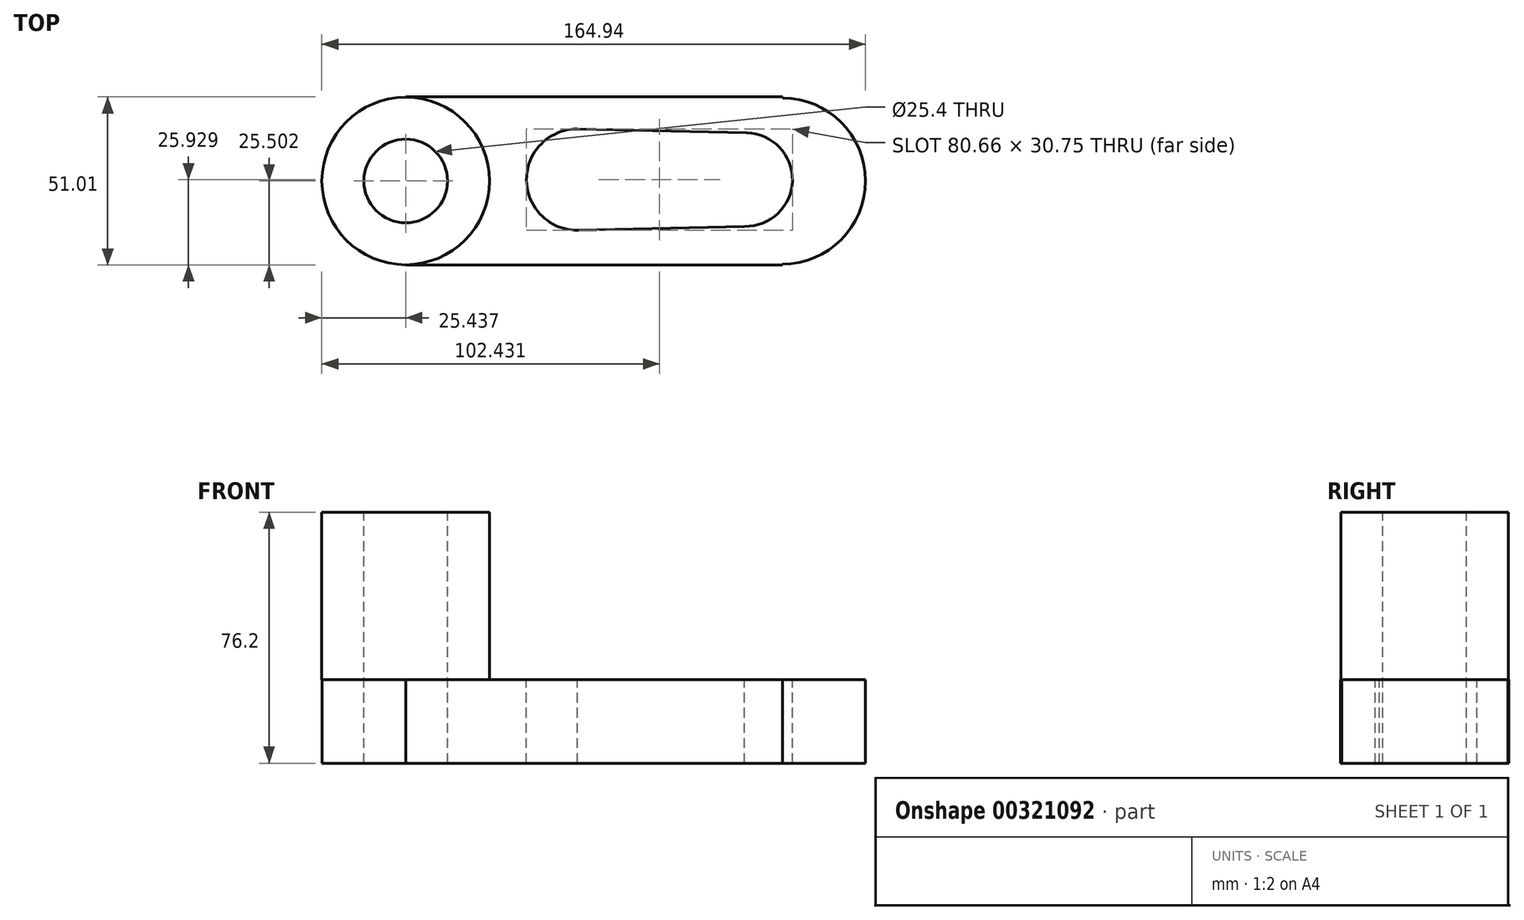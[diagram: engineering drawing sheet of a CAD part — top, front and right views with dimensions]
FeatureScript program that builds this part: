
annotation { "Feature Type Name" : "Feature", "Feature Type Description" : "" }
export const myFeature = defineFeature(function(context is Context, id is Id, definition is map)
    precondition{}
    {
        {
            var Q0;
            Q0=qCreatedBy(makeId("Top.planeOp"),FACE);
            var sketch = newSketch(context, id + "F0", { "sketchPlane" : qUnion([Q0])});
            skLineSegment(sketch, "E0.bottom", {"start": v(-52.04, 27.92) * mm, "end": v(62.26, 27.92) * mm});
            skLineSegment(sketch, "E0.top", {"start": v(-52.04, -23.1) * mm, "end": v(62.26, -23.1) * mm});
            skLineSegment(sketch, "E0.left", {"start": v(-52.04, 27.92) * mm, "end": v(-52.04, 27.77) * mm});
            skLineSegment(sketch, "E0.right", {"start": v(62.26, 27.92) * mm, "end": v(62.26, 27.61) * mm});
            skArc(sketch, "E1", {"start": v(-52.04, 27.77) * mm, "mid": v(-77.4, 2.41) * mm, "end": v(-52.04, -22.95) * mm});
            skArc(sketch, "E2", {"start": v(62.26, -22.79) * mm, "mid": v(87.46, 2.41) * mm, "end": v(62.26, 27.61) * mm});
            skLineSegment(sketch, "E3.trimOffspring", {"start": v(-52.04, -22.95) * mm, "end": v(-52.04, -23.1) * mm});
            skLineSegment(sketch, "E4.trimOffspring", {"start": v(62.26, -22.79) * mm, "end": v(62.26, -23.1) * mm});
            skSolve(sketch);
        }
        {
            var Q0;
            Q0 = qSketchRegion(id + "F0", true);
            extrude(context, id + "F1", {"entities" : qUnion([Q0]), "depth" : 25.4 * mm});
        }
        {
            var Q0;
            Q0=makeQuery(id+"F1.opExtrude","CAP_FACE",FACE,{"disambiguationData":[OSD([sQuery(id+"F0.wireOp",EDGE,"E0.bottom"),sQuery(id+"F0.wireOp",EDGE,"E0.top"),sQuery(id+"F0.wireOp",EDGE,"E0.left"),sQuery(id+"F0.wireOp",EDGE,"E0.right"),sQuery(id+"F0.wireOp",EDGE,"E1"),sQuery(id+"F0.wireOp",EDGE,"E2"),sQuery(id+"F0.wireOp",EDGE,"E3.trimOffspring"),sQuery(id+"F0.wireOp",EDGE,"E4.trimOffspring")])],"isStart":false});
            var sketch = newSketch(context, id + "F2", { "sketchPlane" : qUnion([Q0])});
            skCircle(sketch, "E5", {"center": v(-52.04, 2.41) * mm, "radius": 25.43 * mm});
            skSolve(sketch);
        }
        {
            var Q0;
            Q0 = qSketchRegion(id + "F2", true);
            extrude(context, id + "F3", {"entities" : qUnion([Q0]), "operationType" : NewBodyOperationType.ADD, "depth" : 50.8 * mm});
        }
        {
            var Q0;
            Q0=makeQuery(id+"F3.opExtrude","CAP_FACE",FACE,{"disambiguationData":[OSD([sQuery(id+"F2.wireOp",EDGE,"E5")])],"isStart":false});
            var sketch = newSketch(context, id + "F4", { "sketchPlane" : qUnion([Q0])});
            skCircle(sketch, "E6", {"center": v(-52.04, 2.41) * mm, "radius": 12.7 * mm});
            skSolve(sketch);
        }
        {
            var Q0;
            Q0=makeQuery(id+"F4.imprint","IMPRINT",FACE,{"disambiguationData":[TD([[makeQuery(id+"F4.imprint","IMPRINT",EDGE,{"derivedFrom":sQuery(id+"F4.wireOp",EDGE,"E6")}),1.0]])]});
            extrude(context, id + "F5", {"entities" : qUnion([Q0]), "operationType" : NewBodyOperationType.REMOVE, "oppositeDirection" : true, "depth" : 177.8 * mm});
        }
        {
            var Q0;
            Q0=makeQuery(id+"F1.opExtrude","CAP_FACE",FACE,{"disambiguationData":[OSD([sQuery(id+"F0.wireOp",EDGE,"E0.bottom"),sQuery(id+"F0.wireOp",EDGE,"E0.top"),sQuery(id+"F0.wireOp",EDGE,"E0.left"),sQuery(id+"F0.wireOp",EDGE,"E0.right"),sQuery(id+"F0.wireOp",EDGE,"E1"),sQuery(id+"F0.wireOp",EDGE,"E2"),sQuery(id+"F0.wireOp",EDGE,"E3.trimOffspring"),sQuery(id+"F0.wireOp",EDGE,"E4.trimOffspring")])],"isStart":false});
            var sketch = newSketch(context, id + "F6", { "sketchPlane" : qUnion([Q0])});
            skArc(sketch, "E7", {"start": v(0.71, 18.2) * mm, "mid": v(-15.38, 3.01) * mm, "end": v(0.36, -12.54) * mm});
            skArc(sketch, "E8", {"start": v(50.77, -11.35) * mm, "mid": v(65.28, 2.5) * mm, "end": v(51.43, 17.02) * mm});
            skLineSegment(sketch, "E9", {"start": v(0, 18.22) * mm, "end": v(51.43, 17.02) * mm});
            skLineSegment(sketch, "E10", {"start": v(50.77, -11.35) * mm, "end": v(0.36, -12.54) * mm});
            skSolve(sketch);
        }
        {
            var Q0;
            {var subQ0=sQuery(id+"F6.wireOp",EDGE,"E9");var subQ1=sQuery(id+"F6.wireOp",EDGE,"E7");var subQ2=makeQuery(id+"F6.imprint","INTERSECT",VERTEX,{"disambiguationData":[OD(0.0)],"derivedFrom":[subQ1,subQ0]});Q0=makeQuery(id+"F6.imprint","IMPRINT",FACE,{"disambiguationData":[TD([[makeQuery(id+"F6.imprint","IMPRINT",EDGE,{"disambiguationData":[TD([[subQ2,-1.0]])],"derivedFrom":subQ1}),1.0]])]});}
            var Q1;
            {var subQ3=sQuery(id+"F6.wireOp",EDGE,"E8");Q1=makeQuery(id+"F6.imprint","IMPRINT",FACE,{"disambiguationData":[TD([[makeQuery(id+"F6.imprint","IMPRINT",EDGE,{"derivedFrom":subQ3}),1.0]])]});}
            extrude(context, id + "F7", {"entities" : qUnion([Q0, Q1]), "operationType" : NewBodyOperationType.REMOVE, "oppositeDirection" : true, "depth" : 203.2 * mm});
        }
    });
